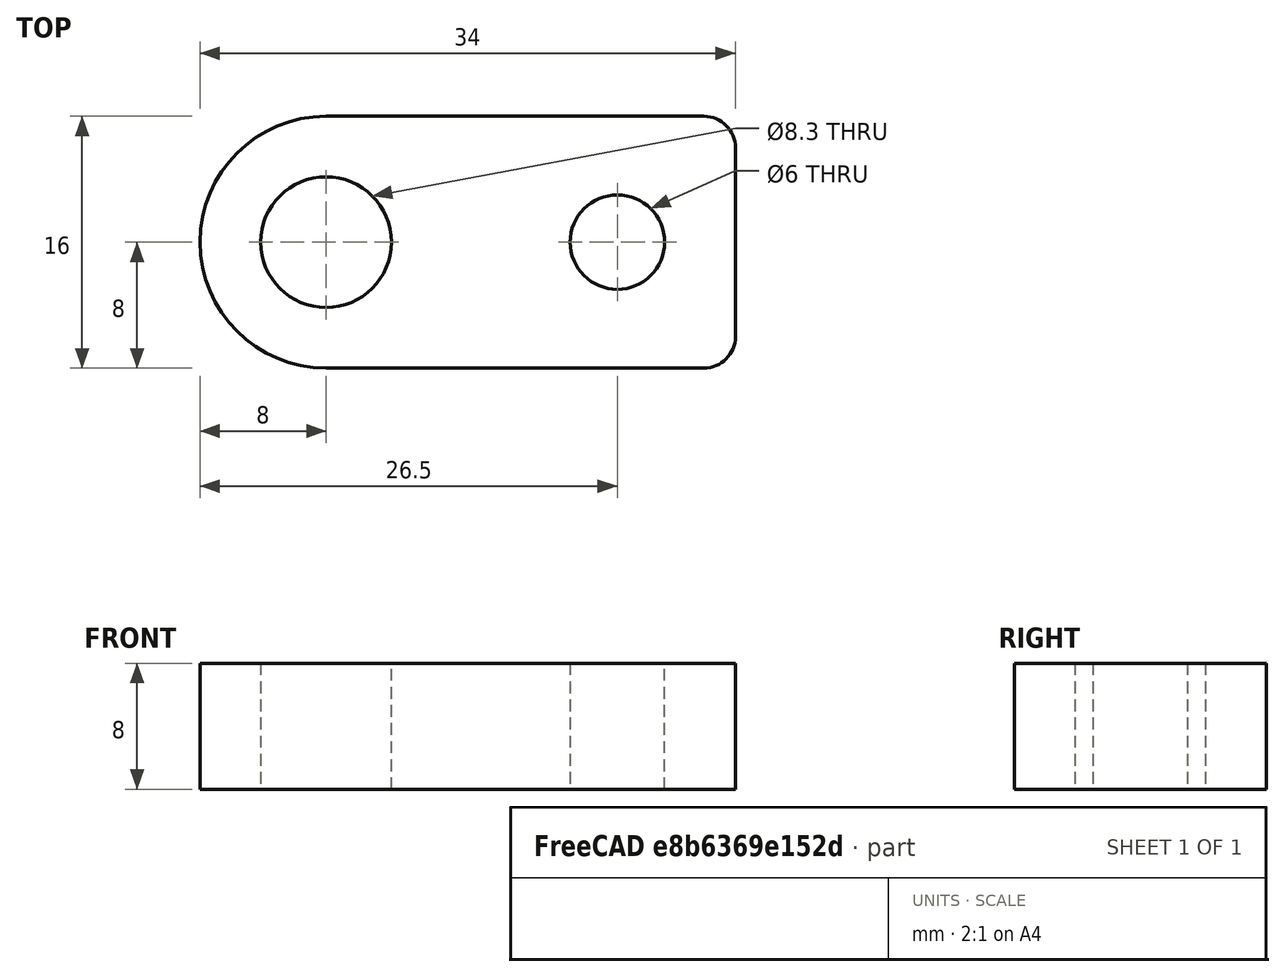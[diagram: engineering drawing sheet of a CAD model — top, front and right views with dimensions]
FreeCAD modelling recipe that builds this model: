
FCSTD DOCUMENT  (FreeCAD 0.19R24366 (Git))
Label: Gas strut coupling adapter non slotted
License: All rights reserved
LicenseURL: http://en.wikipedia.org/wiki/All_rights_reserved
objects: Sketcher::SketchObject×1, PartDesign::Pad×1, PartDesign::Body×1
note: 4 computed .brp shape members not serialized (recipe doc carries the construction recipe); baked Part::Feature solids carry a one-line shape summary decoded from their .brp

FEATURE [Sketcher::SketchObject] Sketch
  FullyConstrained = true
  MapMode = 5
  Support = -> [XY_Plane]
  sketch-geometry (12):
    g0: Circle CenterX=18.5 CenterY=0 CenterZ=0 NormalX=0 NormalY=0 NormalZ=1 AngleXU=0 Radius=3
    g1: LineSegment StartX=-1.3e-15 StartY=8 StartZ=0 EndX=24 EndY=8 EndZ=0
    g2: LineSegment StartX=26 StartY=6 StartZ=0 EndX=26 EndY=-6 EndZ=0
    g3: LineSegment StartX=24 StartY=-8 StartZ=0 EndX=0 EndY=-8 EndZ=0
    g4: ArcOfCircle CenterX=24 CenterY=6 CenterZ=0 NormalX=0 NormalY=0 NormalZ=1 AngleXU=0 Radius=2 StartAngle=0 EndAngle=1.5708
    g5: ArcOfCircle CenterX=24 CenterY=-6 CenterZ=0 NormalX=0 NormalY=0 NormalZ=1 AngleXU=0 Radius=2 StartAngle=4.71239 EndAngle=6.28319
    g6: ArcOfCircle CenterX=0 CenterY=0 CenterZ=0 NormalX=0 NormalY=0 NormalZ=1 AngleXU=0 Radius=8 StartAngle=1.5708 EndAngle=4.71239
    g7: Circle CenterX=18.5 CenterY=0 CenterZ=0 NormalX=0 NormalY=0 NormalZ=1 AngleXU=0 Radius=11.5
    g8: Circle CenterX=0 CenterY=0 CenterZ=0 NormalX=0 NormalY=0 NormalZ=1 AngleXU=0 Radius=6.5
    g9: Circle CenterX=0 CenterY=0 CenterZ=0 NormalX=0 NormalY=0 NormalZ=1 AngleXU=0 Radius=4.15
    g10: LineSegment StartX=18.5 StartY=3 StartZ=0 EndX=18.5 EndY=-3 EndZ=0
    g11: LineSegment StartX=15.5 StartY=0 StartZ=0 EndX=21.5 EndY=0 EndZ=0
  constraints (31):
    c: PointOnObject(g0,g-1)
    c: Horizontal(g1)
    c: Horizontal(g3)
    c: Vertical(g2)
    c: Tangent(g1,g4) = 1.5708
    c: Tangent(g2,g4) = 1.5708
    c: Tangent(g2,g5) = 1.5708
    c: Tangent(g3,g5) = 1.5708
    c: DistanceX(g0,g2) = 7.5
    c: Equal(g5,g4)
    c: Radius(g5) = 2
    c: DistanceY(g3,g1) = 16
    c: Tangent(g6,g1) = 1.5708
    c: Tangent(g3,g6) = 1.5708
    c: Coincident(g7,g0)
    c: Radius(g7) = 11.5
    c: Coincident(g9,g-1)
    c: Coincident(g6,g9)
    c: DistanceX(g6,g0) = 18.5
    c: Coincident(g8,g6)
    c: PointOnObject(g10,g0)
    c: PointOnObject(g10,g0)
    c: Vertical(g10)
    c: PointOnObject(g11,g0)
    c: PointOnObject(g11,g0)
    c: Horizontal(g11)
    c: Diameter(g0) = 6
    c: PointOnObject(g0,g11)
    c: PointOnObject(g0,g10)
    c: Diameter(g9) = 8.3
    c: Diameter(g8) = 13
FEATURE [PartDesign::Pad] Pad  label="Plate thickness"
  Direction = (1,1,1)
  Length = 8
  Length2 = 100
  Midplane = true
  Profile = -> Sketch
  Type = 0
FEATURE [PartDesign::Body] Body
  Group = -> [Sketch,Pad]
  Origin = -> Origin
  Tip = -> Pad
